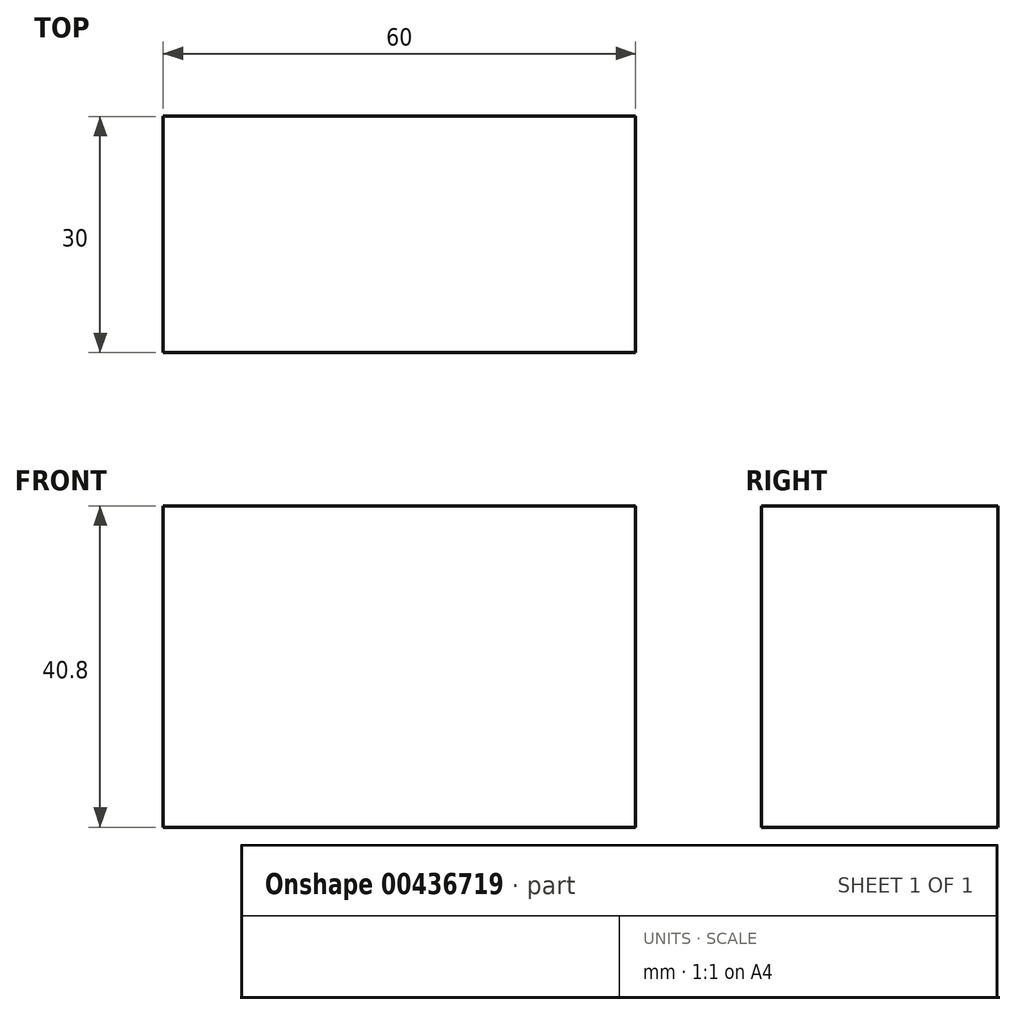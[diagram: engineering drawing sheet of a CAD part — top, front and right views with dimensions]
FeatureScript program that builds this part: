
annotation { "Feature Type Name" : "Feature", "Feature Type Description" : "" }
export const myFeature = defineFeature(function(context is Context, id is Id, definition is map)
    precondition{}
    {
        {
            var Q0;
            Q0=qCreatedBy(makeId("Top.planeOp"),FACE);
            var sketch = newSketch(context, id + "F0", { "sketchPlane" : qUnion([Q0])});
            skLineSegment(sketch, "E0.bottom", {"start": v(-17.34, 12.82) * mm, "end": v(42.66, 12.82) * mm});
            skLineSegment(sketch, "E0.top", {"start": v(-17.34, -17.18) * mm, "end": v(42.66, -17.18) * mm});
            skLineSegment(sketch, "E0.left", {"start": v(-17.34, 12.82) * mm, "end": v(-17.34, -17.18) * mm});
            skLineSegment(sketch, "E0.right", {"start": v(42.66, 12.82) * mm, "end": v(42.66, -17.18) * mm});
            skSolve(sketch);
        }
        {
            var Q0;
            Q0=makeQuery(id+"F0.imprint","IMPRINT",FACE,{"disambiguationData":[TD([[makeQuery(id+"F0.imprint","IMPRINT",EDGE,{"derivedFrom":sQuery(id+"F0.wireOp",EDGE,"E0.bottom")}),-1.0]])]});
            extrude(context, id + "F1", {"entities" : qUnion([Q0]), "depth" : 40.8 * mm});
        }
    });
